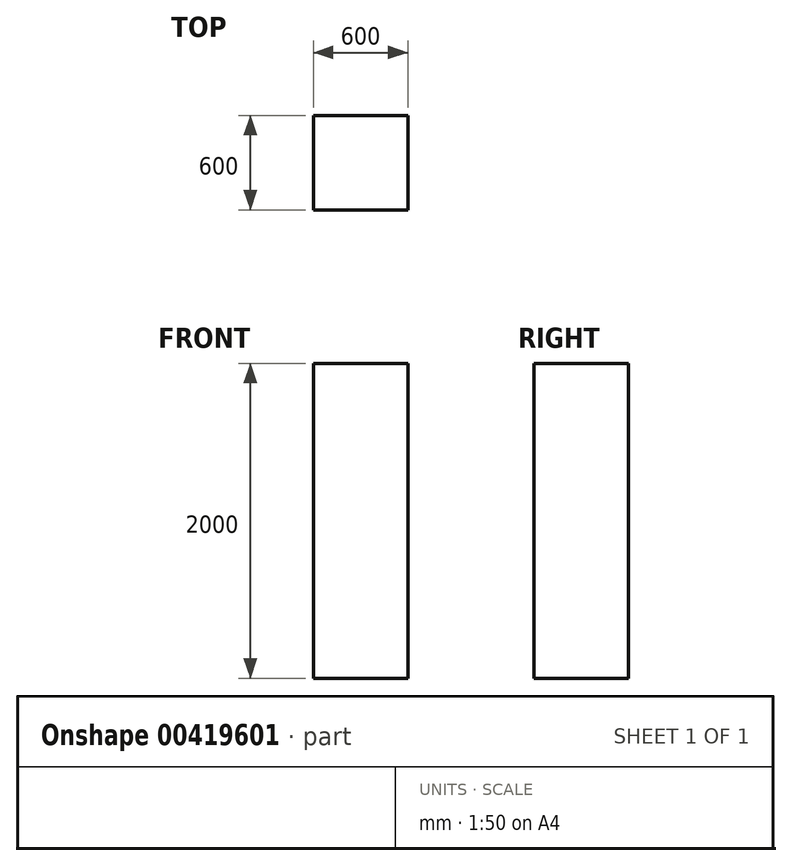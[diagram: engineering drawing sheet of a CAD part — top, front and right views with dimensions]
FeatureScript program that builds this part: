
annotation { "Feature Type Name" : "Feature", "Feature Type Description" : "" }
export const myFeature = defineFeature(function(context is Context, id is Id, definition is map)
    precondition{}
    {
        {
            var Q0;
            Q0=qCreatedBy(makeId("Top.planeOp"),FACE);
            var sketch = newSketch(context, id + "F0", { "sketchPlane" : qUnion([Q0])});
            skLineSegment(sketch, "E0.bottom", {"start": v(-510.45, 541.13) * mm, "end": v(89.55, 541.13) * mm});
            skLineSegment(sketch, "E0.top", {"start": v(-510.45, -58.87) * mm, "end": v(89.55, -58.87) * mm});
            skLineSegment(sketch, "E0.left", {"start": v(-510.45, 541.13) * mm, "end": v(-510.45, -58.87) * mm});
            skLineSegment(sketch, "E0.right", {"start": v(89.55, 541.13) * mm, "end": v(89.55, -58.87) * mm});
            skSolve(sketch);
        }
        {
            var Q0;
            Q0=makeQuery(id+"F0.imprint","IMPRINT",FACE,{"disambiguationData":[TD([[makeQuery(id+"F0.imprint","IMPRINT",EDGE,{"derivedFrom":sQuery(id+"F0.wireOp",EDGE,"E0.bottom")}),-1.0]])]});
            extrude(context, id + "F1", {"entities" : qUnion([Q0]), "depth" : 2000 * mm});
        }
    });
